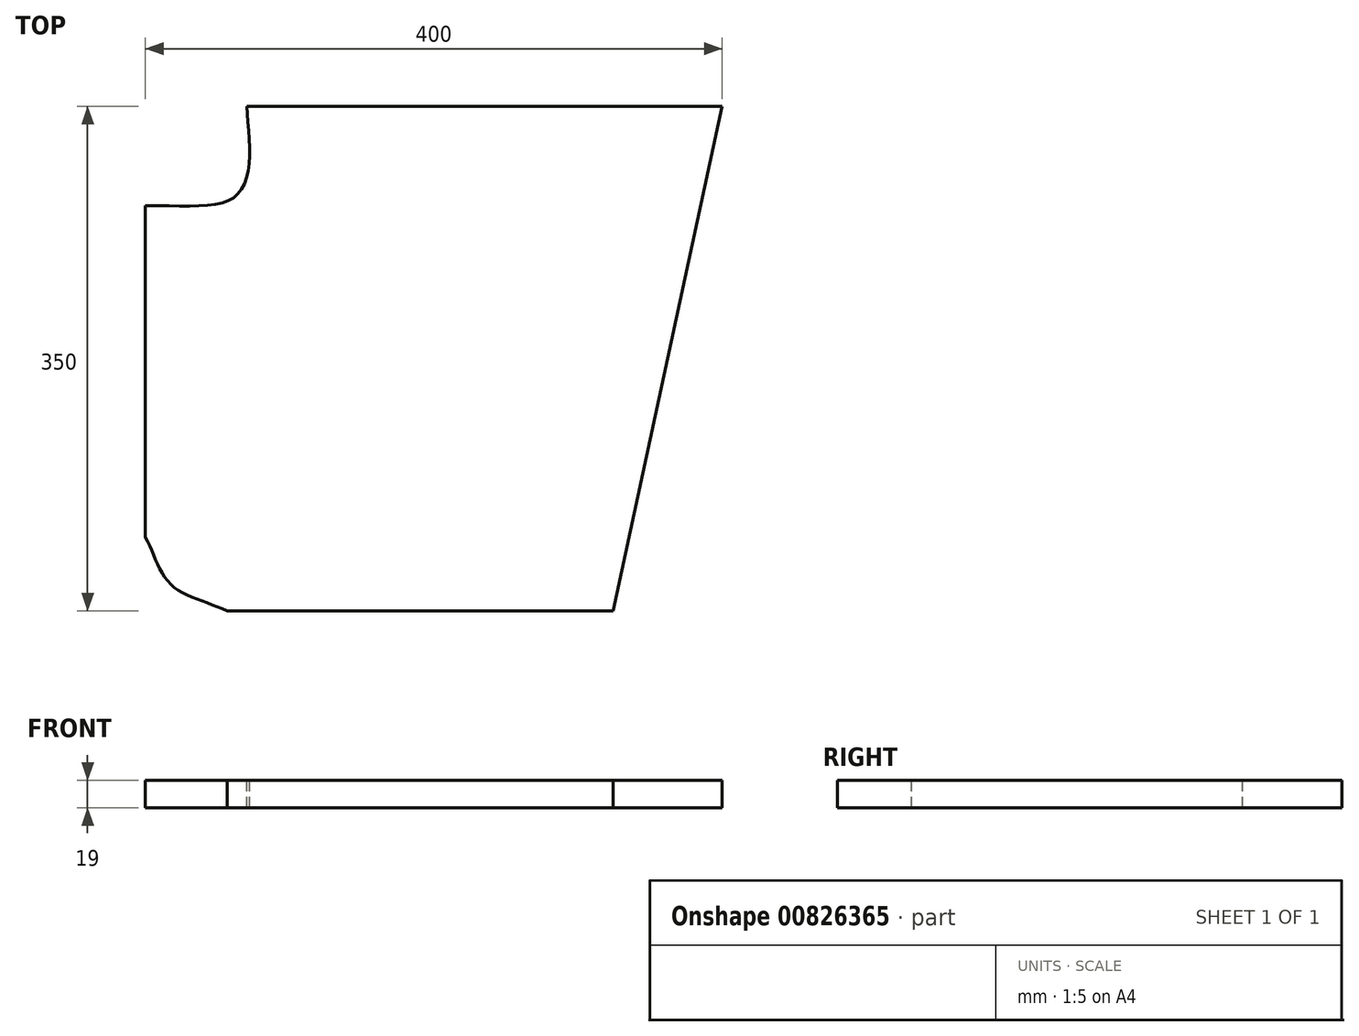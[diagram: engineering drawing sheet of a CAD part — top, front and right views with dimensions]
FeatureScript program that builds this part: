
annotation { "Feature Type Name" : "Feature", "Feature Type Description" : "" }
export const myFeature = defineFeature(function(context is Context, id is Id, definition is map)
    precondition{}
    {
        {
            var Q0;
            Q0=qCreatedBy(makeId("Top.planeOp"),FACE);
            var sketch = newSketch(context, id + "F0", { "sketchPlane" : qUnion([Q0])});
            skLineSegment(sketch, "E0.bottom", {"start": v(200, -175) * mm, "end": v(-200, -175) * mm});
            skLineSegment(sketch, "E0.top", {"start": v(200, 175) * mm, "end": v(-200, 175) * mm});
            skLineSegment(sketch, "E0.left", {"start": v(200, -175) * mm, "end": v(200, 175) * mm});
            skLineSegment(sketch, "E0.right", {"start": v(-200, -175) * mm, "end": v(-200, 175) * mm});
            skPoint(sketch, "E0.middle", {"position": v(0, 0) * mm});
            skSolve(sketch);
        }
        {
            var Q0;
            Q0=makeQuery(id+"F0.imprint","IMPRINT",FACE,{"disambiguationData":[TD([[makeQuery(id+"F0.imprint","IMPRINT",EDGE,{"derivedFrom":sQuery(id+"F0.wireOp",EDGE,"E0.bottom")}),-1.0]])]});
            extrude(context, id + "F1", {"entities" : qUnion([Q0]), "depth" : 19 * mm, "offsetDistance" : 25 * mm});
        }
        {
            var Q0;
            Q0=makeQuery(id+"F1.opExtrude","CAP_FACE",FACE,{"disambiguationData":[OSD([sQuery(id+"F0.wireOp",EDGE,"E0.bottom"),sQuery(id+"F0.wireOp",EDGE,"E0.top"),sQuery(id+"F0.wireOp",EDGE,"E0.left"),sQuery(id+"F0.wireOp",EDGE,"E0.right")])],"isStart":false});
            var sketch = newSketch(context, id + "F2", { "sketchPlane" : qUnion([Q0])});
            skFitSpline(sketch, "E1", {"points": [v(-200, 105.9) * mm, v(-142.33, 109.57) * mm, v(-128.7, 130.01) * mm, v(-129.75, 175) * mm], "startDerivative": vector(198.51, 4.05) * mm, "endDerivative": vector(-8.65, 117.92) * mm});
            skSolve(sketch);
        }
        {
            var Q0;
            {var subQ0=sQuery(id+"F2.wireOp",EDGE,"E1");Q0=makeQuery(id+"F2.imprint","IMPRINT",FACE,{"disambiguationData":[TD([[makeQuery(id+"F2.imprint","IMPRINT",EDGE,{"derivedFrom":subQ0}),1.0]])]});}
            extrude(context, id + "F3", {"entities" : qUnion([Q0]), "operationType" : NewBodyOperationType.REMOVE, "endBound" : BoundingType.THROUGH_ALL, "oppositeDirection" : true, "depth" : 25 * mm, "offsetDistance" : 25 * mm});
        }
        {
            var Q0;
            Q0=makeQuery(id+"F1.opExtrude","CAP_FACE",FACE,{"disambiguationData":[OSD([sQuery(id+"F0.wireOp",EDGE,"E0.bottom"),sQuery(id+"F0.wireOp",EDGE,"E0.top"),sQuery(id+"F0.wireOp",EDGE,"E0.left"),sQuery(id+"F0.wireOp",EDGE,"E0.right")])],"isStart":false});
            var sketch = newSketch(context, id + "F4", { "sketchPlane" : qUnion([Q0])});
            skFitSpline(sketch, "E2", {"points": [v(200, 175) * mm, v(124.5, -175) * mm], "startDerivative": vector(-75.5, -350) * mm, "endDerivative": vector(-75.5, -350) * mm});
            skFitSpline(sketch, "E3", {"points": [v(200, -175) * mm, v(124.5, -175) * mm], "startDerivative": vector(-75.5, 0) * mm, "endDerivative": vector(-75.5, 0) * mm});
            skFitSpline(sketch, "E4", {"points": [v(200, 175) * mm, v(200, -175) * mm], "startDerivative": vector(0, -350) * mm, "endDerivative": vector(0, -350) * mm});
            skSolve(sketch);
        }
        {
            var Q0;
            Q0=makeQuery(id+"F4.imprint","IMPRINT",FACE,{"disambiguationData":[TD([[makeQuery(id+"F4.imprint","IMPRINT",EDGE,{"derivedFrom":sQuery(id+"F4.wireOp",EDGE,"E2")}),1.0]])]});
            extrude(context, id + "F5", {"entities" : qUnion([Q0]), "operationType" : NewBodyOperationType.REMOVE, "endBound" : BoundingType.THROUGH_ALL, "oppositeDirection" : true, "depth" : 25 * mm, "offsetDistance" : 25 * mm});
        }
        {
            var Q0;
            Q0=makeQuery(id+"F1.opExtrude","CAP_FACE",FACE,{"disambiguationData":[OSD([sQuery(id+"F0.wireOp",EDGE,"E0.bottom"),sQuery(id+"F0.wireOp",EDGE,"E0.top"),sQuery(id+"F0.wireOp",EDGE,"E0.left"),sQuery(id+"F0.wireOp",EDGE,"E0.right")])],"isStart":false});
            var sketch = newSketch(context, id + "F6", { "sketchPlane" : qUnion([Q0])});
            skFitSpline(sketch, "E5", {"points": [v(-200, -123.72) * mm, v(-182.18, -156.75) * mm, v(-143.38, -175) * mm], "startDerivative": vector(36.26, -65.88) * mm, "endDerivative": vector(76.41, -37.08) * mm});
            skSolve(sketch);
        }
        {
            var Q0;
            {var subQ0=sQuery(id+"F6.wireOp",EDGE,"E5");Q0=makeQuery(id+"F6.imprint","IMPRINT",FACE,{"disambiguationData":[TD([[makeQuery(id+"F6.imprint","IMPRINT",EDGE,{"derivedFrom":subQ0}),-1.0]])]});}
            extrude(context, id + "F7", {"entities" : qUnion([Q0]), "operationType" : NewBodyOperationType.REMOVE, "endBound" : BoundingType.THROUGH_ALL, "oppositeDirection" : true, "depth" : 25 * mm, "offsetDistance" : 25 * mm});
        }
    });
